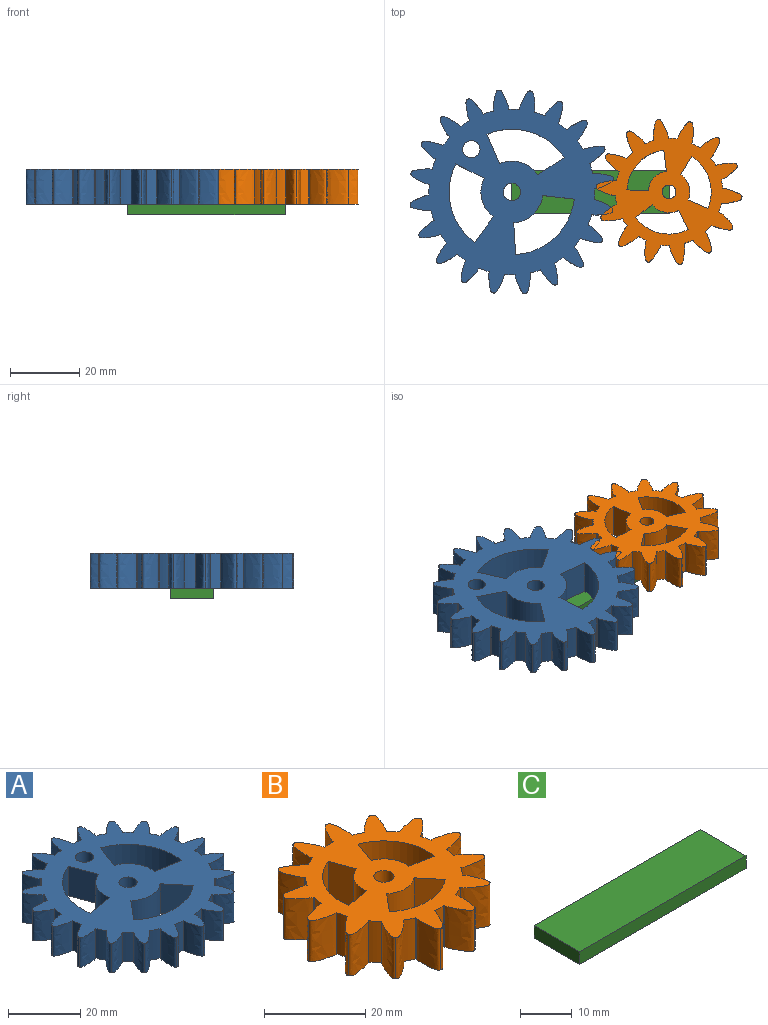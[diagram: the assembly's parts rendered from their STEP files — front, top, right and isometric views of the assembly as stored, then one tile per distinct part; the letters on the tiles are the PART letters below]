
ASSEMBLY  parts=3 mates=2
PART A: 116 faces, bbox 59.3x59.3x10 mm
  f0: plane 59.26x59.26mm, normal (0,0,1), area 1603.5mm2, adj f2,f3,f4,f5,f6,f7,f8,f9
  f1: plane 59.26x59.26mm, normal (0,0,-1), area 1603.5mm2, adj f2,f3,f4,f5,f6,f7,f8,f9
  f2: plane 10x0.22mm, normal (0,1,0), area 2.2mm2, adj f0,f1,f4,f6
  f3: plane 10x0.22mm, normal (0,-1,0), area 2.2mm2, adj f0,f1,f5,f11
  f4: extruded ~10x5.57mm, area 63mm2, adj f0,f1,f2,f5
  f5: extruded ~10x5.57mm, area 63mm2, adj f0,f1,f3,f4
  f6: cylinder r=23.92mm len=10mm, axis (0,0,-1), area 31.2mm2, adj f0,f1,f2,f98
  f7: plane 10x0.21mm, normal (-0.31,0.95,0), area 2.2mm2, adj f0,f1,f9,f11
  f8: plane 10x0.21mm, normal (0.31,-0.95,0), area 2.2mm2, adj f0,f1,f10,f16
  f9: extruded ~10x4.68mm, area 63mm2, adj f0,f1,f7,f10
  f10: extruded ~10x5.97mm, area 63mm2, adj f0,f1,f8,f9
  f11: cylinder r=23.92mm len=10mm, axis (0,0,-1), area 31.2mm2, adj f0,f1,f3,f7
  f12: plane 10x0.18mm, normal (-0.59,0.81,0), area 2.2mm2, adj f0,f1,f14,f16
  f13: plane 10x0.18mm, normal (0.59,-0.81,0), area 2.2mm2, adj f0,f1,f15,f21
  f14: extruded ~10x5.05mm, area 63mm2, adj f0,f1,f12,f15
  f15: extruded ~10x5.79mm, area 63mm2, adj f0,f1,f13,f14
  f16: cylinder r=23.92mm len=10mm, axis (0,0,-1), area 31.2mm2, adj f0,f1,f8,f12
  f17: plane 10x0.18mm, normal (-0.81,0.59,0), area 2.2mm2, adj f0,f1,f19,f21
  f18: plane 10x0.18mm, normal (0.81,-0.59,0), area 2.2mm2, adj f0,f1,f20,f26
  f19: extruded ~10x5.79mm, area 63mm2, adj f0,f1,f17,f20
  f20: extruded ~10x5.05mm, area 63mm2, adj f0,f1,f18,f19
  f21: cylinder r=23.92mm len=10mm, axis (0,0,-1), area 31.2mm2, adj f0,f1,f13,f17
  f22: plane 10x0.21mm, normal (-0.95,0.31,0), area 2.2mm2, adj f0,f1,f24,f26
  f23: plane 10x0.21mm, normal (0.95,-0.31,0), area 2.2mm2, adj f0,f1,f25,f31
  f24: extruded ~10x5.97mm, area 63mm2, adj f0,f1,f22,f25
  f25: extruded ~10x4.68mm, area 63mm2, adj f0,f1,f23,f24
  f26: cylinder r=23.92mm len=10mm, axis (0,0,-1), area 31.2mm2, adj f0,f1,f18,f22
  f27: plane 10x0.22mm, normal (-1,0,0), area 2.2mm2, adj f0,f1,f29,f31
  f28: plane 10x0.22mm, normal (1,0,0), area 2.2mm2, adj f0,f1,f30,f36
  f29: extruded ~10x5.57mm, area 63mm2, adj f0,f1,f27,f30
  f30: extruded ~10x5.57mm, area 63mm2, adj f0,f1,f28,f29
  f31: cylinder r=23.92mm len=10mm, axis (0,0,-1), area 31.2mm2, adj f0,f1,f23,f27
  f32: plane 10x0.21mm, normal (-0.95,-0.31,0), area 2.2mm2, adj f0,f1,f34,f36
  f33: plane 10x0.21mm, normal (0.95,0.31,0), area 2.2mm2, adj f0,f1,f35,f41
  f34: extruded ~10x4.68mm, area 63mm2, adj f0,f1,f32,f35
  f35: extruded ~10x5.97mm, area 63mm2, adj f0,f1,f33,f34
  f36: cylinder r=23.92mm len=10mm, axis (0,0,-1), area 31.2mm2, adj f0,f1,f28,f32
  f37: plane 10x0.18mm, normal (-0.81,-0.59,0), area 2.2mm2, adj f0,f1,f39,f41
  f38: plane 10x0.18mm, normal (0.81,0.59,0), area 2.2mm2, adj f0,f1,f40,f46
  f39: extruded ~10x5.05mm, area 63mm2, adj f0,f1,f37,f40
  f40: extruded ~10x5.79mm, area 63mm2, adj f0,f1,f38,f39
  f41: cylinder r=23.92mm len=10mm, axis (0,0,-1), area 31.2mm2, adj f0,f1,f33,f37
  f42: plane 10x0.18mm, normal (-0.59,-0.81,0), area 2.2mm2, adj f0,f1,f44,f46
  f43: plane 10x0.18mm, normal (0.59,0.81,0), area 2.2mm2, adj f0,f1,f45,f51
  f44: extruded ~10x5.79mm, area 63mm2, adj f0,f1,f42,f45
  f45: extruded ~10x5.05mm, area 63mm2, adj f0,f1,f43,f44
  f46: cylinder r=23.92mm len=10mm, axis (0,0,-1), area 31.2mm2, adj f0,f1,f38,f42
  f47: plane 10x0.21mm, normal (-0.31,-0.95,0), area 2.2mm2, adj f0,f1,f49,f51
  f48: plane 10x0.21mm, normal (0.31,0.95,0), area 2.2mm2, adj f0,f1,f50,f56
  f49: extruded ~10x5.97mm, area 63mm2, adj f0,f1,f47,f50
  f50: extruded ~10x4.68mm, area 63mm2, adj f0,f1,f48,f49
  f51: cylinder r=23.92mm len=10mm, axis (0,0,-1), area 31.2mm2, adj f0,f1,f43,f47
  f52: plane 10x0.22mm, normal (0,-1,0), area 2.2mm2, adj f0,f1,f54,f56
  f53: plane 10x0.22mm, normal (0,1,0), area 2.2mm2, adj f0,f1,f55,f61
  f54: extruded ~10x5.57mm, area 63mm2, adj f0,f1,f52,f55
  f55: extruded ~10x5.57mm, area 63mm2, adj f0,f1,f53,f54
  f56: cylinder r=23.92mm len=10mm, axis (0,0,-1), area 31.2mm2, adj f0,f1,f48,f52
  f57: plane 10x0.21mm, normal (0.31,-0.95,0), area 2.2mm2, adj f0,f1,f59,f61
  f58: plane 10x0.21mm, normal (-0.31,0.95,0), area 2.2mm2, adj f0,f1,f60,f66
  f59: extruded ~10x4.68mm, area 63mm2, adj f0,f1,f57,f60
  f60: extruded ~10x5.97mm, area 63mm2, adj f0,f1,f58,f59
  f61: cylinder r=23.92mm len=10mm, axis (0,0,-1), area 31.2mm2, adj f0,f1,f53,f57
  f62: plane 10x0.18mm, normal (0.59,-0.81,0), area 2.2mm2, adj f0,f1,f64,f66
  f63: plane 10x0.18mm, normal (-0.59,0.81,0), area 2.2mm2, adj f0,f1,f65,f71
  f64: extruded ~10x5.05mm, area 63mm2, adj f0,f1,f62,f65
  f65: extruded ~10x5.79mm, area 63mm2, adj f0,f1,f63,f64
  f66: cylinder r=23.92mm len=10mm, axis (0,0,-1), area 31.2mm2, adj f0,f1,f58,f62
  f67: plane 10x0.18mm, normal (0.81,-0.59,0), area 2.2mm2, adj f0,f1,f69,f71
  f68: plane 10x0.18mm, normal (-0.81,0.59,0), area 2.2mm2, adj f0,f1,f70,f76
  f69: extruded ~10x5.79mm, area 63mm2, adj f0,f1,f67,f70
  f70: extruded ~10x5.05mm, area 63mm2, adj f0,f1,f68,f69
  f71: cylinder r=23.92mm len=10mm, axis (0,0,-1), area 31.2mm2, adj f0,f1,f63,f67
  f72: plane 10x0.21mm, normal (0.95,-0.31,0), area 2.2mm2, adj f0,f1,f74,f76
  f73: plane 10x0.21mm, normal (-0.95,0.31,0), area 2.2mm2, adj f0,f1,f75,f81
  f74: extruded ~10x5.97mm, area 63mm2, adj f0,f1,f72,f75
  f75: extruded ~10x4.68mm, area 63mm2, adj f0,f1,f73,f74
  f76: cylinder r=23.92mm len=10mm, axis (0,0,-1), area 31.2mm2, adj f0,f1,f68,f72
  f77: plane 10x0.22mm, normal (1,0,0), area 2.2mm2, adj f0,f1,f79,f81
  f78: plane 10x0.22mm, normal (-1,0,0), area 2.2mm2, adj f0,f1,f80,f86
  f79: extruded ~10x5.57mm, area 63mm2, adj f0,f1,f77,f80
  f80: extruded ~10x5.57mm, area 63mm2, adj f0,f1,f78,f79
  f81: cylinder r=23.92mm len=10mm, axis (0,0,-1), area 31.2mm2, adj f0,f1,f73,f77
  f82: plane 10x0.21mm, normal (0.95,0.31,0), area 2.2mm2, adj f0,f1,f84,f86
  f83: plane 10x0.21mm, normal (-0.95,-0.31,0), area 2.2mm2, adj f0,f1,f85,f91
  f84: extruded ~10x4.68mm, area 63mm2, adj f0,f1,f82,f85
  f85: extruded ~10x5.97mm, area 63mm2, adj f0,f1,f83,f84
  f86: cylinder r=23.92mm len=10mm, axis (0,0,-1), area 31.2mm2, adj f0,f1,f78,f82
  f87: plane 10x0.18mm, normal (0.81,0.59,0), area 2.2mm2, adj f0,f1,f89,f91
  f88: plane 10x0.18mm, normal (-0.81,-0.59,0), area 2.2mm2, adj f0,f1,f90,f96
  f89: extruded ~10x5.05mm, area 63mm2, adj f0,f1,f87,f90
  f90: extruded ~10x5.79mm, area 63mm2, adj f0,f1,f88,f89
  f91: cylinder r=23.92mm len=10mm, axis (0,0,-1), area 31.2mm2, adj f0,f1,f83,f87
  f92: plane 10x0.18mm, normal (0.59,0.81,0), area 2.2mm2, adj f0,f1,f94,f96
  f93: plane 10x0.18mm, normal (-0.59,-0.81,0), area 2.2mm2, adj f0,f1,f95,f101
  f94: extruded ~10x5.79mm, area 63mm2, adj f0,f1,f92,f95
  f95: extruded ~10x5.05mm, area 63mm2, adj f0,f1,f93,f94
  f96: cylinder r=23.92mm len=10mm, axis (0,0,-1), area 31.2mm2, adj f0,f1,f88,f92
  f97: plane 10x0.21mm, normal (0.31,0.95,0), area 2.2mm2, adj f0,f1,f99,f101
  f98: plane 10x0.21mm, normal (-0.31,-0.95,0), area 2.2mm2, adj f0,f1,f6,f100
  f99: extruded ~10x5.97mm, area 63mm2, adj f0,f1,f97,f100
  f100: extruded ~10x4.68mm, area 63mm2, adj f0,f1,f98,f99
  f101: cylinder r=23.92mm len=10mm, axis (0,0,-1), area 31.2mm2, adj f0,f1,f93,f97
  f102: cylinder r=8.93mm len=10mm, axis (0,0,1), area 124.7mm2, adj f0,f1,f103,f104
  f103: plane 10x8.61mm, normal (-0.94,-0.34,0), area 91.6mm2, adj f0,f1,f102,f105
  f104: plane 10x9.02mm, normal (-0.17,0.98,0), area 91.6mm2, adj f0,f1,f102,f105
  f105: cylinder r=18.09mm len=20.14mm, axis (0,0,1), area 252.6mm2, adj f0,f1,f103,f104
  f106: cylinder r=8.93mm len=10mm, axis (0,0,1), area 124.7mm2, adj f0,f1,f107,f108
  f107: plane 10x9.02mm, normal (0.17,0.98,0), area 91.6mm2, adj f0,f1,f106,f109
  f108: plane 10x8.61mm, normal (0.94,-0.34,0), area 91.6mm2, adj f0,f1,f106,f109
  f109: cylinder r=18.09mm len=20.14mm, axis (0,0,1), area 252.6mm2, adj f0,f1,f107,f108
  f110: plane 10x7.02mm, normal (0.77,-0.64,0), area 91.6mm2, adj f0,f1,f111,f112
  f111: cylinder r=8.93mm len=11.48mm, axis (0,0,1), area 124.7mm2, adj f0,f1,f110,f113
  f112: cylinder r=18.09mm len=23.26mm, axis (0,0,1), area 252.6mm2, adj f0,f1,f110,f113
  f113: plane 10x7.02mm, normal (-0.77,-0.64,0), area 91.6mm2, adj f0,f1,f111,f112
  f114: cylinder r=2.5mm len=10mm, axis (0,0,1), area 157.1mm2, adj f0,f1
  f115: cylinder r=2.5mm len=10mm, axis (0,0,1), area 157.1mm2, adj f0,f1
PART B: 85 faces, bbox 42.2x41.5x10 mm
  f0: plane 42.2x41.51mm, normal (0,0,1), area 757.3mm2, adj f2,f3,f4,f5,f6,f7,f8,f9
  f1: plane 42.2x41.51mm, normal (0,0,-1), area 757.3mm2, adj f2,f3,f4,f5,f6,f7,f8,f9
  f2: plane 10x0.17mm, normal (0,1,0), area 1.7mm2, adj f0,f1,f4,f6
  f3: plane 10x0.17mm, normal (0,-1,0), area 1.7mm2, adj f0,f1,f5,f11
  f4: extruded ~10x5.57mm, area 63mm2, adj f0,f1,f2,f5
  f5: extruded ~10x5.57mm, area 63mm2, adj f0,f1,f3,f4
  f6: cylinder r=15.5mm len=10mm, axis (0,0,-1), area 25.6mm2, adj f0,f1,f2,f68
  f7: plane 10x0.16mm, normal (-0.43,0.9,0), area 1.7mm2, adj f0,f1,f9,f11
  f8: plane 10x0.16mm, normal (0.43,-0.9,0), area 1.7mm2, adj f0,f1,f10,f16
  f9: extruded ~10x4.39mm, area 63mm2, adj f0,f1,f7,f10
  f10: extruded ~10x5.97mm, area 63mm2, adj f0,f1,f8,f9
  f11: cylinder r=15.5mm len=10mm, axis (0,0,-1), area 25.6mm2, adj f0,f1,f3,f7
  f12: plane 10x0.14mm, normal (-0.78,0.62,0), area 1.7mm2, adj f0,f1,f14,f16
  f13: plane 10x0.14mm, normal (0.78,-0.62,0), area 1.7mm2, adj f0,f1,f15,f21
  f14: extruded ~10x5.72mm, area 63mm2, adj f0,f1,f12,f15
  f15: extruded ~10x5.18mm, area 63mm2, adj f0,f1,f13,f14
  f16: cylinder r=15.5mm len=10mm, axis (0,0,-1), area 25.6mm2, adj f0,f1,f8,f12
  f17: plane 10x0.17mm, normal (-0.97,0.22,0), area 1.7mm2, adj f0,f1,f19,f21
  f18: plane 10x0.17mm, normal (0.97,-0.22,0), area 1.7mm2, adj f0,f1,f20,f26
  f19: extruded ~10x5.91mm, area 63mm2, adj f0,f1,f17,f20
  f20: extruded ~10x4.98mm, area 63mm2, adj f0,f1,f18,f19
  f21: cylinder r=15.5mm len=10mm, axis (0,0,-1), area 25.6mm2, adj f0,f1,f13,f17
  f22: plane 10x0.17mm, normal (-0.97,-0.22,0), area 1.7mm2, adj f0,f1,f24,f26
  f23: plane 10x0.17mm, normal (0.97,0.22,0), area 1.7mm2, adj f0,f1,f25,f31
  f24: extruded ~10x4.98mm, area 63mm2, adj f0,f1,f22,f25
  f25: extruded ~10x5.91mm, area 63mm2, adj f0,f1,f23,f24
  f26: cylinder r=15.5mm len=10mm, axis (0,0,-1), area 25.6mm2, adj f0,f1,f18,f22
  f27: plane 10x0.14mm, normal (-0.78,-0.62,0), area 1.7mm2, adj f0,f1,f29,f31
  f28: plane 10x0.14mm, normal (0.78,0.62,0), area 1.7mm2, adj f0,f1,f30,f36
  f29: extruded ~10x5.18mm, area 63mm2, adj f0,f1,f27,f30
  f30: extruded ~10x5.72mm, area 63mm2, adj f0,f1,f28,f29
  f31: cylinder r=15.5mm len=10mm, axis (0,0,-1), area 25.6mm2, adj f0,f1,f23,f27
  f32: plane 10x0.16mm, normal (-0.43,-0.9,0), area 1.7mm2, adj f0,f1,f34,f36
  f33: plane 10x0.16mm, normal (0.43,0.9,0), area 1.7mm2, adj f0,f1,f35,f41
  f34: extruded ~10x5.97mm, area 63mm2, adj f0,f1,f32,f35
  f35: extruded ~10x4.39mm, area 63mm2, adj f0,f1,f33,f34
  f36: cylinder r=15.5mm len=10mm, axis (0,0,-1), area 25.6mm2, adj f0,f1,f28,f32
  f37: plane 10x0.17mm, normal (0,-1,0), area 1.7mm2, adj f0,f1,f39,f41
  f38: plane 10x0.17mm, normal (0,1,0), area 1.7mm2, adj f0,f1,f40,f46
  f39: extruded ~10x5.57mm, area 63mm2, adj f0,f1,f37,f40
  f40: extruded ~10x5.57mm, area 63mm2, adj f0,f1,f38,f39
  f41: cylinder r=15.5mm len=10mm, axis (0,0,-1), area 25.6mm2, adj f0,f1,f33,f37
  f42: plane 10x0.16mm, normal (0.43,-0.9,0), area 1.7mm2, adj f0,f1,f44,f46
  f43: plane 10x0.16mm, normal (-0.43,0.9,0), area 1.7mm2, adj f0,f1,f45,f51
  f44: extruded ~10x4.39mm, area 63mm2, adj f0,f1,f42,f45
  f45: extruded ~10x5.97mm, area 63mm2, adj f0,f1,f43,f44
  f46: cylinder r=15.5mm len=10mm, axis (0,0,-1), area 25.6mm2, adj f0,f1,f38,f42
  f47: plane 10x0.14mm, normal (0.78,-0.62,0), area 1.7mm2, adj f0,f1,f49,f51
  f48: plane 10x0.14mm, normal (-0.78,0.62,0), area 1.7mm2, adj f0,f1,f50,f56
  f49: extruded ~10x5.72mm, area 63mm2, adj f0,f1,f47,f50
  f50: extruded ~10x5.18mm, area 63mm2, adj f0,f1,f48,f49
  f51: cylinder r=15.5mm len=10mm, axis (0,0,-1), area 25.6mm2, adj f0,f1,f43,f47
  f52: plane 10x0.17mm, normal (0.97,-0.22,0), area 1.7mm2, adj f0,f1,f54,f56
  f53: plane 10x0.17mm, normal (-0.97,0.22,0), area 1.7mm2, adj f0,f1,f55,f61
  f54: extruded ~10x5.91mm, area 63mm2, adj f0,f1,f52,f55
  f55: extruded ~10x4.98mm, area 63mm2, adj f0,f1,f53,f54
  f56: cylinder r=15.5mm len=10mm, axis (0,0,-1), area 25.6mm2, adj f0,f1,f48,f52
  f57: plane 10x0.17mm, normal (0.97,0.22,0), area 1.7mm2, adj f0,f1,f59,f61
  f58: plane 10x0.17mm, normal (-0.97,-0.22,0), area 1.7mm2, adj f0,f1,f60,f66
  f59: extruded ~10x4.98mm, area 63mm2, adj f0,f1,f57,f60
  f60: extruded ~10x5.91mm, area 63mm2, adj f0,f1,f58,f59
  f61: cylinder r=15.5mm len=10mm, axis (0,0,-1), area 25.6mm2, adj f0,f1,f53,f57
  f62: plane 10x0.14mm, normal (0.78,0.62,0), area 1.7mm2, adj f0,f1,f64,f66
  f63: plane 10x0.14mm, normal (-0.78,-0.62,0), area 1.7mm2, adj f0,f1,f65,f71
  f64: extruded ~10x5.18mm, area 63mm2, adj f0,f1,f62,f65
  f65: extruded ~10x5.72mm, area 63mm2, adj f0,f1,f63,f64
  f66: cylinder r=15.5mm len=10mm, axis (0,0,-1), area 25.6mm2, adj f0,f1,f58,f62
  f67: plane 10x0.16mm, normal (0.43,0.9,0), area 1.7mm2, adj f0,f1,f69,f71
  f68: plane 10x0.16mm, normal (-0.43,-0.9,0), area 1.7mm2, adj f0,f1,f6,f70
  f69: extruded ~10x5.97mm, area 63mm2, adj f0,f1,f67,f70
  f70: extruded ~10x4.39mm, area 63mm2, adj f0,f1,f68,f69
  f71: cylinder r=15.5mm len=10mm, axis (0,0,-1), area 25.6mm2, adj f0,f1,f63,f67
  f72: cylinder r=6mm len=10mm, axis (0,0,1), area 83.8mm2, adj f0,f1,f73,f74
  f73: plane 10x5.78mm, normal (-0.94,-0.34,0), area 61.5mm2, adj f0,f1,f72,f75
  f74: plane 10x6.06mm, normal (-0.17,0.98,0), area 61.5mm2, adj f0,f1,f72,f75
  f75: cylinder r=12.15mm len=13.53mm, axis (0,0,1), area 169.7mm2, adj f0,f1,f73,f74
  f76: plane 10x4.71mm, normal (0.77,-0.64,0), area 61.5mm2, adj f0,f1,f77,f78
  f77: cylinder r=6mm len=10mm, axis (0,0,1), area 83.8mm2, adj f0,f1,f76,f79
  f78: cylinder r=12.15mm len=15.62mm, axis (0,0,1), area 169.7mm2, adj f0,f1,f76,f79
  f79: plane 10x4.71mm, normal (-0.77,-0.64,0), area 61.5mm2, adj f0,f1,f77,f78
  f80: cylinder r=6mm len=10mm, axis (0,0,1), area 83.8mm2, adj f0,f1,f81,f82
  f81: plane 10x6.06mm, normal (0.17,0.98,0), area 61.5mm2, adj f0,f1,f80,f83
  f82: plane 10x5.78mm, normal (0.94,-0.34,0), area 61.5mm2, adj f0,f1,f80,f83
  f83: cylinder r=12.15mm len=13.53mm, axis (0,0,1), area 169.7mm2, adj f0,f1,f81,f82
  f84: cylinder r=2mm len=10mm, axis (0,0,1), area 125.7mm2, adj f0,f1
PART C: 6 faces, bbox 45.3x12.4x3 mm
  f0: plane 12.43x3mm, normal (1,0,0), area 37.3mm2, adj f1,f3,f4,f5
  f1: plane 45.32x3mm, normal (0,1,0), area 136mm2, adj f0,f2,f4,f5
  f2: plane 12.43x3mm, normal (-1,0,0), area 37.3mm2, adj f1,f3,f4,f5
  f3: plane 45.32x3mm, normal (0,-1,0), area 136mm2, adj f0,f2,f4,f5
  f4: plane 45.32x12.43mm, normal (0,0,-1), area 563.2mm2, adj f0,f1,f2,f3
  f5: plane 45.32x12.43mm, normal (0,0,1), area 563.2mm2, adj f0,f1,f2,f3
PLACE A rot(axis=(0.37,-0.93,0),180deg) t=(-22.66,0,10)mm
PLACE B rot(axis=(-0.92,-0.4,0),180deg) t=(22.66,0,10)mm
PLACE C at identity
MATE revolute B.f6 <-> C.f5  axis (0,0,-1) through (22.66,0,0)mm
MATE revolute A.f6 <-> C.f5  axis (0,0,-1) through (-22.66,0,0)mm
